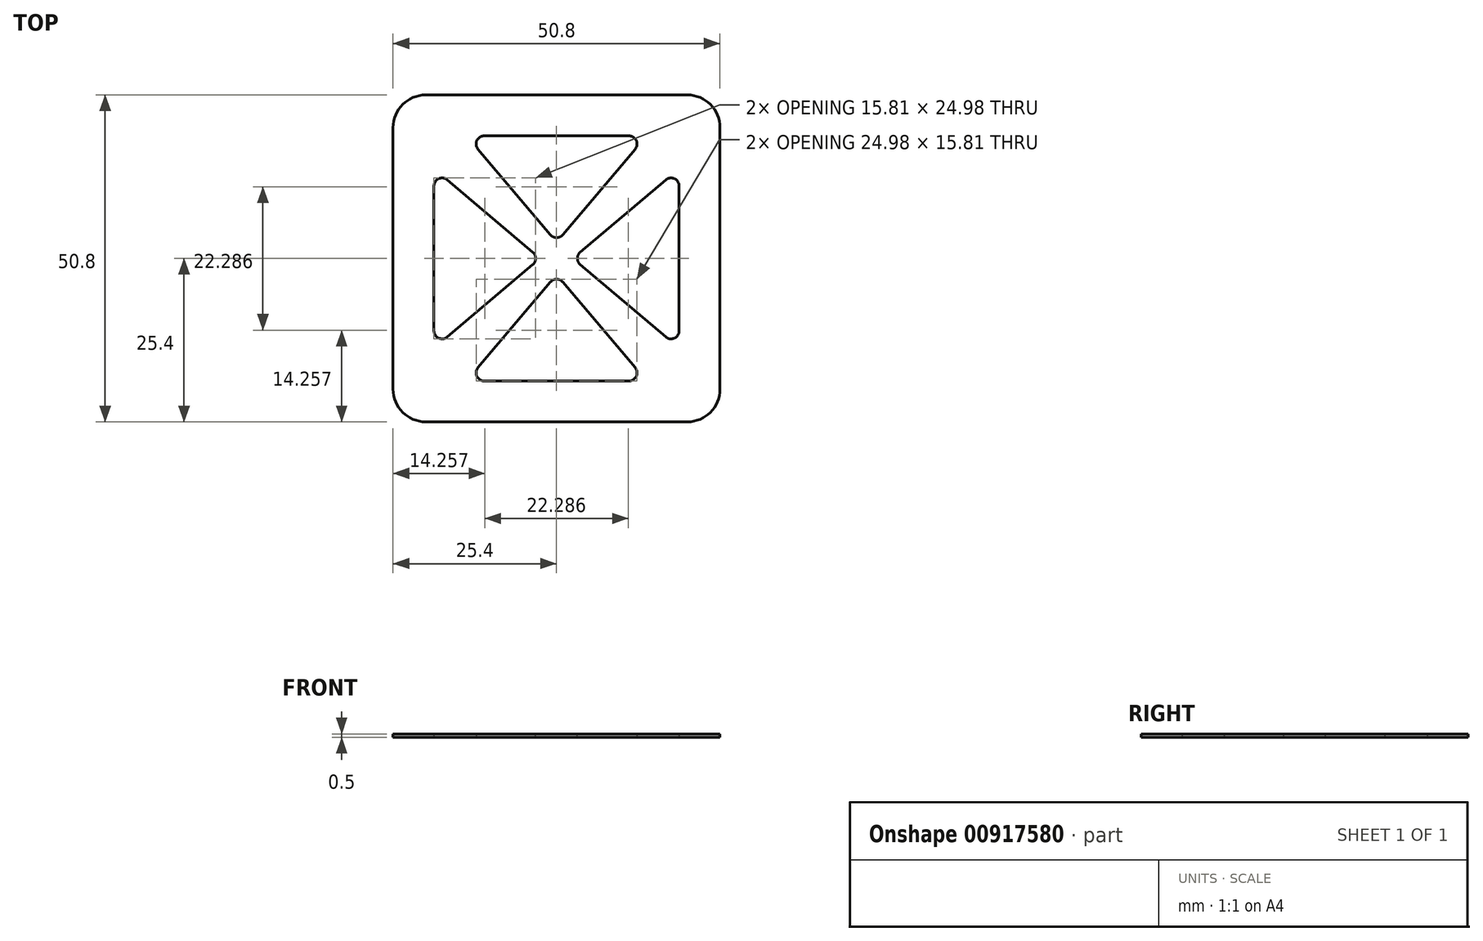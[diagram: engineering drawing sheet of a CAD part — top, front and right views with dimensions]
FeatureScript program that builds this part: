
annotation { "Feature Type Name" : "Feature", "Feature Type Description" : "" }
export const myFeature = defineFeature(function(context is Context, id is Id, definition is map)
    precondition{}
    {
        {
            var Q0;
            Q0=qCreatedBy(makeId("Top.planeOp"),FACE);
            var sketch = newSketch(context, id + "F0", { "sketchPlane" : qUnion([Q0])});
            skLineSegment(sketch, "E0.bottom", {"start": v(25.4, 25.4) * mm, "end": v(-25.4, 25.4) * mm});
            skLineSegment(sketch, "E0.top", {"start": v(25.4, -25.4) * mm, "end": v(-25.4, -25.4) * mm});
            skLineSegment(sketch, "E0.left", {"start": v(25.4, 25.4) * mm, "end": v(25.4, -25.4) * mm});
            skLineSegment(sketch, "E0.right", {"start": v(-25.4, 25.4) * mm, "end": v(-25.4, -25.4) * mm});
            skPoint(sketch, "E0.middle", {"position": v(0, 0) * mm});
            skLineSegment(sketch, "E1.bottom", {"start": v(2.54, 2.54) * mm, "end": v(-2.54, 2.54) * mm, "construction": true});
            skLineSegment(sketch, "E1.top", {"start": v(2.54, -2.54) * mm, "end": v(-2.54, -2.54) * mm, "construction": true});
            skLineSegment(sketch, "E1.left", {"start": v(2.54, 2.54) * mm, "end": v(2.54, -2.54) * mm, "construction": true});
            skLineSegment(sketch, "E1.right", {"start": v(-2.54, 2.54) * mm, "end": v(-2.54, -2.54) * mm, "construction": true});
            skLineSegment(sketch, "E2", {"start": v(13.97, -19.05) * mm, "end": v(0, -2.54) * mm});
            skLineSegment(sketch, "E3", {"start": v(2.54, -2.54) * mm, "end": v(2.54, 0) * mm});
            skLineSegment(sketch, "E4", {"start": v(2.54, 0) * mm, "end": v(19.05, -13.97) * mm});
            skLineSegment(sketch, "E5.1.0", {"start": v(19.05, 13.97) * mm, "end": v(2.54, 0) * mm});
            skLineSegment(sketch, "E5.1.1", {"start": v(0, 2.54) * mm, "end": v(13.97, 19.05) * mm});
            skLineSegment(sketch, "E5.2.0", {"start": v(-13.97, 19.05) * mm, "end": v(0, 2.54) * mm});
            skLineSegment(sketch, "E5.2.1", {"start": v(-2.54, 0) * mm, "end": v(-19.05, 13.97) * mm});
            skLineSegment(sketch, "E5.3.0", {"start": v(-19.05, -13.97) * mm, "end": v(-2.54, 0) * mm});
            skLineSegment(sketch, "E5.3.1", {"start": v(0, -2.54) * mm, "end": v(-13.97, -19.05) * mm});
            skLineSegment(sketch, "E6", {"start": v(-13.97, -19.05) * mm, "end": v(13.97, -19.05) * mm});
            skLineSegment(sketch, "E7", {"start": v(19.05, -13.97) * mm, "end": v(19.05, 13.97) * mm});
            skLineSegment(sketch, "E8", {"start": v(-19.05, -13.97) * mm, "end": v(-19.05, 13.97) * mm});
            skLineSegment(sketch, "E9", {"start": v(-13.97, 19.05) * mm, "end": v(13.97, 19.05) * mm});
            skSolve(sketch);
        }
        {
            var Q0;
            Q0=makeQuery(id+"F0.imprint","IMPRINT",FACE,{"disambiguationData":[TD([[makeQuery(id+"F0.imprint","IMPRINT",EDGE,{"derivedFrom":sQuery(id+"F0.wireOp",EDGE,"E0.bottom")}),1.0]])]});
            extrude(context, id + "F1", {"entities" : qUnion([Q0]), "depth" : .5 * mm, "offsetDistance" : 25.4 * mm});
        }
        {
            var Q0;
            Q0=makeQuery(id+"F1.opExtrude","SWEPT_EDGE",EDGE,{"disambiguationData":[OSD([sQuery(id+"F0.wireOp",EDGE,"E2"),sQuery(id+"F0.wireOp",EDGE,"E5.3.1")])]});
            var Q1;
            Q1=makeQuery(id+"F1.opExtrude","SWEPT_EDGE",EDGE,{"disambiguationData":[OSD([sQuery(id+"F0.wireOp",EDGE,"E5.2.1"),sQuery(id+"F0.wireOp",EDGE,"E8")])]});
            var Q2;
            Q2=makeQuery(id+"F1.opExtrude","SWEPT_EDGE",EDGE,{"disambiguationData":[OSD([sQuery(id+"F0.wireOp",EDGE,"E5.3.1"),sQuery(id+"F0.wireOp",EDGE,"E6")])]});
            var Q3;
            Q3=makeQuery(id+"F1.opExtrude","SWEPT_EDGE",EDGE,{"disambiguationData":[OSD([sQuery(id+"F0.wireOp",EDGE,"E4"),sQuery(id+"F0.wireOp",EDGE,"E5.1.0")])]});
            var Q4;
            Q4=makeQuery(id+"F1.opExtrude","SWEPT_EDGE",EDGE,{"disambiguationData":[OSD([sQuery(id+"F0.wireOp",EDGE,"E4"),sQuery(id+"F0.wireOp",EDGE,"E7")])]});
            var Q5;
            Q5=makeQuery(id+"F1.opExtrude","SWEPT_EDGE",EDGE,{"disambiguationData":[OSD([sQuery(id+"F0.wireOp",EDGE,"E2"),sQuery(id+"F0.wireOp",EDGE,"E6")])]});
            var Q6;
            Q6=makeQuery(id+"F1.opExtrude","SWEPT_EDGE",EDGE,{"disambiguationData":[OSD([sQuery(id+"F0.wireOp",EDGE,"E5.2.1"),sQuery(id+"F0.wireOp",EDGE,"E5.3.0")])]});
            var Q7;
            Q7=makeQuery(id+"F1.opExtrude","SWEPT_EDGE",EDGE,{"disambiguationData":[OSD([sQuery(id+"F0.wireOp",EDGE,"E5.1.1"),sQuery(id+"F0.wireOp",EDGE,"E5.2.0")])]});
            var Q8;
            Q8=makeQuery(id+"F1.opExtrude","SWEPT_EDGE",EDGE,{"disambiguationData":[OSD([sQuery(id+"F0.wireOp",EDGE,"E5.1.0"),sQuery(id+"F0.wireOp",EDGE,"E7")])]});
            var Q9;
            Q9=makeQuery(id+"F1.opExtrude","SWEPT_EDGE",EDGE,{"disambiguationData":[OSD([sQuery(id+"F0.wireOp",EDGE,"E5.1.1"),sQuery(id+"F0.wireOp",EDGE,"E9")])]});
            var Q10;
            Q10=makeQuery(id+"F1.opExtrude","SWEPT_EDGE",EDGE,{"disambiguationData":[OSD([sQuery(id+"F0.wireOp",EDGE,"E5.3.0"),sQuery(id+"F0.wireOp",EDGE,"E8")])]});
            var Q11;
            Q11=makeQuery(id+"F1.opExtrude","SWEPT_EDGE",EDGE,{"disambiguationData":[OSD([sQuery(id+"F0.wireOp",EDGE,"E5.2.0"),sQuery(id+"F0.wireOp",EDGE,"E9")])]});
            fillet(context, id + "F2", {"entities" : qUnion([Q0, Q1, Q2, Q3, Q4, Q5, Q6, Q7, Q8, Q9, Q10, Q11]), "radius" : 1.27 * mm, "tangentPropagation" : true, "allowEdgeOverflow" : false});
        }
        {
            var Q0;
            Q0=makeQuery(id+"F1.opExtrude","SWEPT_EDGE",EDGE,{"disambiguationData":[OSD([sQuery(id+"F0.wireOp",EDGE,"E0.bottom"),sQuery(id+"F0.wireOp",EDGE,"E0.left")])]});
            var Q1;
            Q1=makeQuery(id+"F1.opExtrude","SWEPT_EDGE",EDGE,{"disambiguationData":[OSD([sQuery(id+"F0.wireOp",EDGE,"E0.bottom"),sQuery(id+"F0.wireOp",EDGE,"E0.right")])]});
            var Q2;
            Q2=makeQuery(id+"F1.opExtrude","SWEPT_EDGE",EDGE,{"disambiguationData":[OSD([sQuery(id+"F0.wireOp",EDGE,"E0.top"),sQuery(id+"F0.wireOp",EDGE,"E0.right")])]});
            var Q3;
            Q3=makeQuery(id+"F1.opExtrude","SWEPT_EDGE",EDGE,{"disambiguationData":[OSD([sQuery(id+"F0.wireOp",EDGE,"E0.top"),sQuery(id+"F0.wireOp",EDGE,"E0.left")])]});
            fillet(context, id + "F3", {"entities" : qUnion([Q0, Q1, Q2, Q3]), "radius" : 5.08 * mm, "tangentPropagation" : true, "allowEdgeOverflow" : false});
        }
    });
